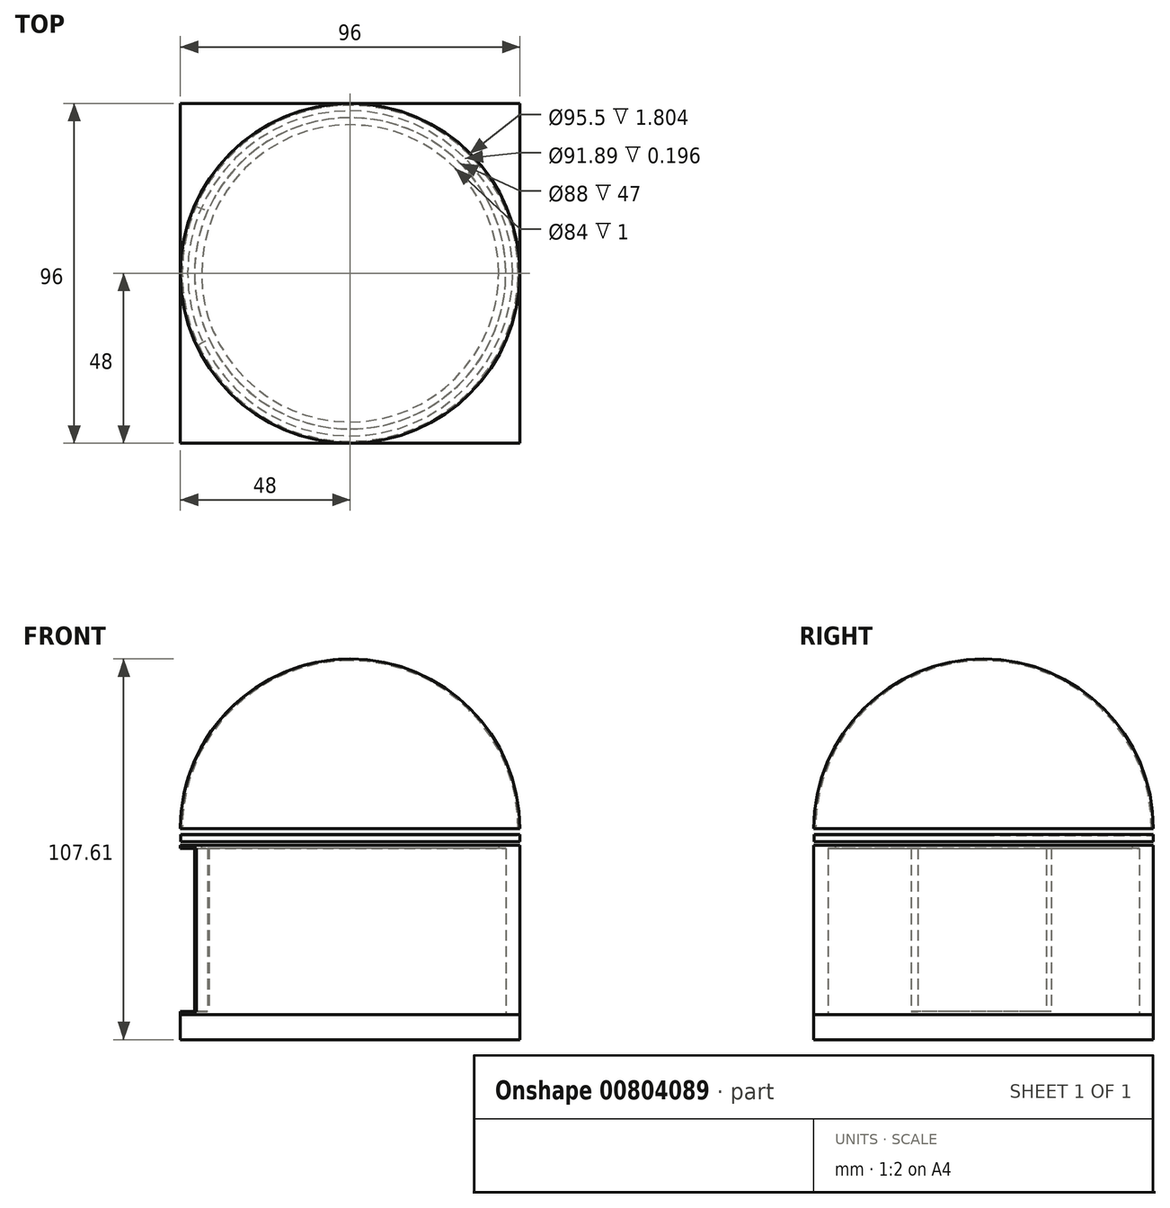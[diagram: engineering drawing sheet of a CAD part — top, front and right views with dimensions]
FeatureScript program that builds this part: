
annotation { "Feature Type Name" : "Feature", "Feature Type Description" : "" }
export const myFeature = defineFeature(function(context is Context, id is Id, definition is map)
    precondition{}
    {
        {
            var Q0;
            Q0=qCreatedBy(makeId("Top.planeOp"),FACE);
            var sketch = newSketch(context, id + "F0", { "sketchPlane" : qUnion([Q0])});
            skLineSegment(sketch, "E0.bottom", {"start": v(-48, 48) * mm, "end": v(48, 48) * mm});
            skLineSegment(sketch, "E0.top", {"start": v(-48, -48) * mm, "end": v(48, -48) * mm});
            skLineSegment(sketch, "E0.left", {"start": v(-48, 48) * mm, "end": v(-48, -48) * mm});
            skLineSegment(sketch, "E0.right", {"start": v(48, 48) * mm, "end": v(48, -48) * mm});
            skPoint(sketch, "E0.middle", {"position": v(0, 0) * mm});
            skSolve(sketch);
        }
        {
            var Q0;
            Q0 = qSketchRegion(id + "F0", true);
            extrude(context, id + "F1", {"entities" : qUnion([Q0]), "depth" : 6 * mm, "offsetDistance" : 25 * mm});
        }
        {
            var Q0;
            Q0=makeQuery(id+"F1.opExtrude","CAP_FACE",FACE,{"disambiguationData":[OSD([sQuery(id+"F0.wireOp",EDGE,"E0.bottom"),sQuery(id+"F0.wireOp",EDGE,"E0.top"),sQuery(id+"F0.wireOp",EDGE,"E0.left"),sQuery(id+"F0.wireOp",EDGE,"E0.right")])],"isStart":false});
            var sketch = newSketch(context, id + "F2", { "sketchPlane" : qUnion([Q0])});
            skLineSegment(sketch, "E1.bottom", {"start": v(-48, -48) * mm, "end": v(48, -48) * mm});
            skLineSegment(sketch, "E1.top", {"start": v(-48, 48) * mm, "end": v(48, 48) * mm});
            skLineSegment(sketch, "E1.left", {"start": v(-48, -48) * mm, "end": v(-48, 48) * mm});
            skLineSegment(sketch, "E1.right", {"start": v(48, -48) * mm, "end": v(48, 48) * mm});
            skPoint(sketch, "E1.middle", {"position": v(0, 0) * mm});
            skSolve(sketch);
        }
        {
            var Q0;
            Q0 = qSketchRegion(id + "F2", true);
            extrude(context, id + "F3", {"entities" : qUnion([Q0]), "operationType" : NewBodyOperationType.ADD, "depth" : 1 * mm, "offsetDistance" : 25 * mm});
        }
        {
            var Q0;
            Q0=makeQuery(id+"F3.opExtrude","CAP_FACE",FACE,{"disambiguationData":[OSD([sQuery(id+"F2.wireOp",EDGE,"E1.bottom"),sQuery(id+"F2.wireOp",EDGE,"E1.top"),sQuery(id+"F2.wireOp",EDGE,"E1.left"),sQuery(id+"F2.wireOp",EDGE,"E1.right")])],"isStart":false});
            var sketch = newSketch(context, id + "F4", { "sketchPlane" : qUnion([Q0])});
            skCircle(sketch, "E2", {"center": v(0, 0) * mm, "radius": 48 * mm});
            skCircle(sketch, "E3", {"center": v(0, 0) * mm, "radius": 44 * mm});
            skSolve(sketch);
        }
        {
            var Q0;
            Q0 = qSketchRegion(id + "F4", true);
            extrude(context, id + "F5", {"entities" : qUnion([Q0]), "operationType" : NewBodyOperationType.ADD, "depth" : 1 * mm, "offsetDistance" : 25 * mm});
        }
        {
            var Q0;
            Q0=makeQuery(id+"F5.opExtrude","CAP_FACE",FACE,{"disambiguationData":[OSD([sQuery(id+"F4.wireOp",EDGE,"E2"),sQuery(id+"F4.wireOp",EDGE,"E3")])],"isStart":false});
            var sketch = newSketch(context, id + "F6", { "sketchPlane" : qUnion([Q0])});
            skArc(sketch, "E4", {"start": v(-44.03, 19.11) * mm, "mid": v(48, 0.75) * mm, "end": v(-43.41, -20.48) * mm});
            skArc(sketch, "E5", {"start": v(-40.27, 17.74) * mm, "mid": v(44, 0.47) * mm, "end": v(-39.88, -18.6) * mm});
            skLineSegment(sketch, "E6", {"start": v(-44.03, 19.11) * mm, "end": v(-40.27, 17.74) * mm});
            skLineSegment(sketch, "E7", {"start": v(-43.41, -20.48) * mm, "end": v(-39.88, -18.6) * mm});
            skSolve(sketch);
        }
        {
            var Q0;
            Q0 = qSketchRegion(id + "F6", true);
            extrude(context, id + "F7", {"entities" : qUnion([Q0]), "operationType" : NewBodyOperationType.ADD, "depth" : 46 * mm, "offsetDistance" : 25 * mm});
        }
        {
            var Q0;
            Q0=makeQuery(id+"F7.opExtrude","CAP_FACE",FACE,{"disambiguationData":[OSD([sQuery(id+"F6.wireOp",EDGE,"E4"),sQuery(id+"F6.wireOp",EDGE,"E5"),sQuery(id+"F6.wireOp",EDGE,"E6"),sQuery(id+"F6.wireOp",EDGE,"E7")])],"isStart":false});
            var sketch = newSketch(context, id + "F8", { "sketchPlane" : qUnion([Q0])});
            skCircle(sketch, "E8", {"center": v(0, 0) * mm, "radius": 48 * mm});
            skCircle(sketch, "E9", {"center": v(0, 0) * mm, "radius": 42 * mm});
            skSolve(sketch);
        }
        {
            var Q0;
            Q0 = qSketchRegion(id + "F8", true);
            extrude(context, id + "F9", {"entities" : qUnion([Q0]), "operationType" : NewBodyOperationType.ADD, "depth" : 1 * mm, "offsetDistance" : 25 * mm});
        }
        {
            var Q0;
            Q0=qCreatedBy(makeId("Front.planeOp"),FACE);
            var sketch = newSketch(context, id + "F10", { "sketchPlane" : qUnion([Q0])});
            skLineSegment(sketch, "E10", {"start": v(-47.95, 55.94) * mm, "end": v(-47.95, 57.94) * mm});
            skLineSegment(sketch, "E11", {"start": v(-47.95, 57.94) * mm, "end": v(-45.95, 57.94) * mm});
            skLineSegment(sketch, "E12", {"start": v(-45.95, 57.94) * mm, "end": v(-45.95, 57.75) * mm});
            skLineSegment(sketch, "E13", {"start": v(-47.95, 55.94) * mm, "end": v(-47.75, 55.94) * mm});
            skLineSegment(sketch, "E14", {"start": v(-47.75, 55.94) * mm, "end": v(-47.75, 57.75) * mm});
            skLineSegment(sketch, "E15", {"start": v(-47.75, 57.75) * mm, "end": v(-45.95, 57.75) * mm});
            skLineSegment(sketch, "E16", {"start": v(0, 0) * mm, "end": v(0, 77.35) * mm});
            skSolve(sketch);
        }
        {
            var Q0;
            Q0=makeQuery(id+"F10.imprint","IMPRINT",FACE,{"disambiguationData":[TD([[makeQuery(id+"F10.imprint","IMPRINT",EDGE,{"derivedFrom":sQuery(id+"F10.wireOp",EDGE,"E10")}),-1.0]])]});
            var Q1;
            Q1=sQuery(id+"F10.wireOp",EDGE,"E16");
            revolve(context, id + "F11", {"surfaceOperationType" : NewSurfaceOperationType.NEW, "entities" : qUnion([Q0]), "axis" : qUnion([Q1]), "revolveType" : RevolveType.FULL});
        }
        {
            var Q0;
            Q0=qCreatedBy(makeId("Front.planeOp"),FACE);
            var sketch = newSketch(context, id + "F12", { "sketchPlane" : qUnion([Q0])});
            skArc(sketch, "E17", {"start": v(-48, 59.6) * mm, "mid": v(-33.94, 93.55) * mm, "end": v(0, 107.6) * mm});
            skArc(sketch, "E18", {"start": v(-47.5, 59.6) * mm, "mid": v(-33.59, 93.2) * mm, "end": v(0, 107.1) * mm});
            skLineSegment(sketch, "E19", {"start": v(0, 107.6) * mm, "end": v(0, 107.1) * mm});
            skLineSegment(sketch, "E20", {"start": v(-48, 59.6) * mm, "end": v(-47.5, 59.6) * mm});
            skLineSegment(sketch, "E21", {"start": v(0, 64.4) * mm, "end": v(0, 88.52) * mm});
            skSolve(sketch);
        }
        {
            var Q0;
            Q0 = qSketchRegion(id + "F12", true);
            var Q1;
            Q1=sQuery(id+"F12.wireOp",EDGE,"E21");
            revolve(context, id + "F13", {"surfaceOperationType" : NewSurfaceOperationType.NEW, "entities" : qUnion([Q0]), "axis" : qUnion([Q1]), "revolveType" : RevolveType.FULL});
        }
        {
            var Q0;
            Q0=qCreatedBy(makeId("Top.planeOp"),FACE);
            var sketch = newSketch(context, id + "F14", { "sketchPlane" : qUnion([Q0])});
            skCircle(sketch, "E22", {"center": v(0, 0) * mm, "radius": 6 * mm});
            skCircle(sketch, "E23", {"center": v(0, 0) * mm, "radius": 5 * mm});
            skSolve(sketch);
        }
        {
            var Q0;
            Q0 = qSketchRegion(id + "F14", true);
            extrude(context, id + "F15", {"entities" : qUnion([Q0]), "operationType" : NewBodyOperationType.ADD, "endBound" : BoundingType.UP_TO_NEXT, "depth" : 8 * mm, "offsetDistance" : 25 * mm});
        }
    });
